# Revit family: 665_Counter_Btw_Jambs_Mtd_Overhead_Door
name_source: partatom
category: Doors
units: mm (PartAtom-declared; Revit-internal decimal feet)

## family parameters
Always vertical = Yes
Cut with Voids When Loaded = No
Host = Wall
OmniClass Number = 23.30.10.17.27.11
OmniClass Title = Overhead Coiling
Room Calculation Point = No
Shared = No

## types (1)
- *See Type Catalog*
    Analytic Construction = <None>
    Assembly Code = B2030410
    Bottom Bar = Wood
    Construction Details = https://www.arcat.com
    Define Thermal Properties by = Schematic Type
    Description = Overhead Door Model 665 Overhead Coiling Wood Counter Door
    Door Gap From Wall Interior = 0' - 7 1/16"
    Door Track Material = Wood - Red Oak
    Electrical Operator = No
    Elevation From Level = 3' - 2 1/2"
    Fire Rating = As Specified in 08 36 00
    Function = Interior
    Green Building-LEED = https://www.arcat.com
    Has End Caps = Yes
    Height = 6' - 11 5/8"
    Hood Material = Wood - White Oak
    Keynote = 08 33 13
    Left End Cap Thickness = 0' - 1"
    Lock Type = [Thumb Turn Locks] [Cylinder Locks]
    Manual Operation = Yes
    Manufacturer = Overhead Door Corporation
    Maximum Height = 8'  0
    Maximum Width = 12'  0
    Model = 665
    Operation = [Awning Crank Operator][Manual - Push Up]
    Operator Material = Wood - Red Oak
    Panel Height = 2' - 10 13/32"
    Panel Material = Wood - White Oak
    Panel Width = 6' - 4 5/8"
    Product Data = http://www.arcat.com
    Right End Cap Thickness = 0' - 1"
    Rough Height = 0' - 0"
    Rough Width = 0' - 0"
    SpecWizard = https://www.arcat.com
    Specification = https://www.arcat.com
    Thickness = 0' - 0 1/2"
    URL = http://www.overheaddoor.com
    Wall Closure = By host
    Width = 6' - 11"

## geometry (parser evidence)
native form markers: Blend x8, Sweep x7
no freeform markers — native parametric forms only
